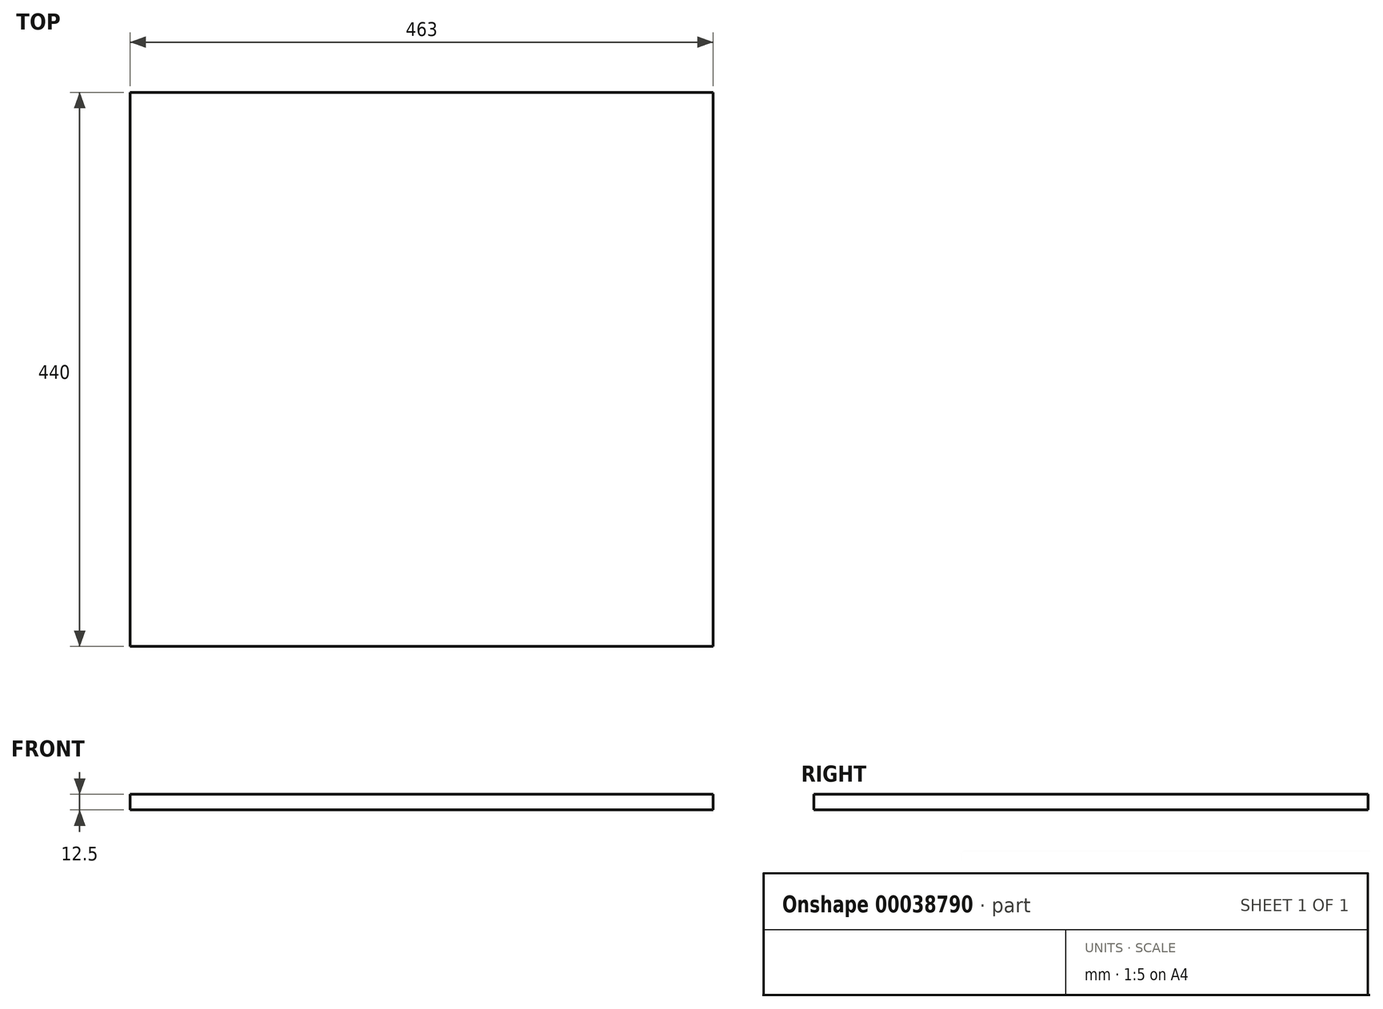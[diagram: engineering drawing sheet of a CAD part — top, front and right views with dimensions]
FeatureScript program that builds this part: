
annotation { "Feature Type Name" : "Feature", "Feature Type Description" : "" }
export const myFeature = defineFeature(function(context is Context, id is Id, definition is map)
    precondition{}
    {
        {
            var Q0;
            Q0=qCreatedBy(makeId("Top.planeOp"),FACE);
            var sketch = newSketch(context, id + "F0", { "sketchPlane" : qUnion([Q0])});
            skLineSegment(sketch, "E0.bottom", {"start": v(-70.96, 65.05) * mm, "end": v(392.04, 65.05) * mm});
            skLineSegment(sketch, "E0.top", {"start": v(-70.96, -374.95) * mm, "end": v(392.04, -374.95) * mm});
            skLineSegment(sketch, "E0.left", {"start": v(-70.96, 65.05) * mm, "end": v(-70.96, -374.95) * mm});
            skLineSegment(sketch, "E0.right", {"start": v(392.04, 65.05) * mm, "end": v(392.04, -374.95) * mm});
            skSolve(sketch);
        }
        {
            var Q0;
            Q0=qSketchRegion(id+"F0",true);
            extrude(context, id + "F1", {"entities" : qUnion([Q0]), "depth" : 12.5 * mm});
        }
    });
